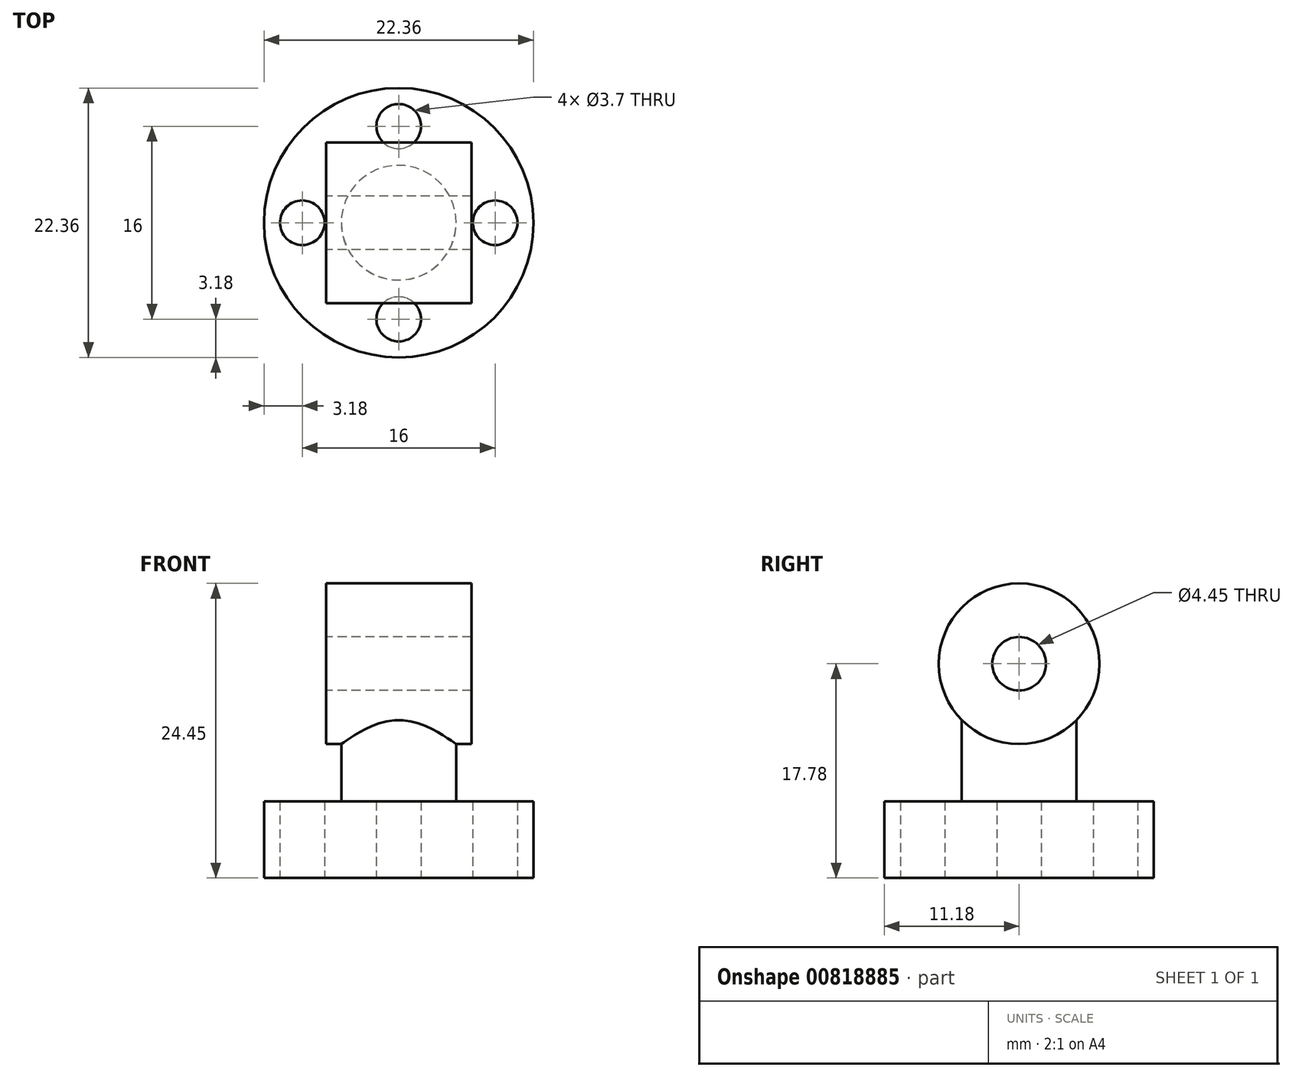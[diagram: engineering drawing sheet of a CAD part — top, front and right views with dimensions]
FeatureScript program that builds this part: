
annotation { "Feature Type Name" : "Feature", "Feature Type Description" : "" }
export const myFeature = defineFeature(function(context is Context, id is Id, definition is map)
    precondition{}
    {
        {
            var Q0;
            Q0=qCreatedBy(makeId("Top.planeOp"),FACE);
            var sketch = newSketch(context, id + "F0", { "sketchPlane" : qUnion([Q0])});
            skCircle(sketch, "E0", {"center": v(0, 0) * mm, "radius": 11.18 * mm});
            skLineSegment(sketch, "E1", {"start": v(0, 0) * mm, "end": v(0, 8) * mm});
            skCircle(sketch, "E2", {"center": v(0, 8) * mm, "radius": 1.85 * mm});
            skCircle(sketch, "E3.1.0", {"center": v(8, 0) * mm, "radius": 1.85 * mm});
            skCircle(sketch, "E3.2.0", {"center": v(0, -8) * mm, "radius": 1.85 * mm});
            skCircle(sketch, "E3.3.0", {"center": v(-8, 0) * mm, "radius": 1.85 * mm});
            skLineSegment(sketch, "E3.anchor1", {"start": v(0, 0) * mm, "end": v(0, 8) * mm, "construction": true});
            skLineSegment(sketch, "E3.anchor2", {"start": v(0, 0) * mm, "end": v(-8, 0) * mm, "construction": true});
            skSolve(sketch);
        }
        {
            var Q0;
            Q0=makeQuery(id+"F0.imprint","IMPRINT",FACE,{"disambiguationData":[TD([[makeQuery(id+"F0.imprint","IMPRINT",EDGE,{"derivedFrom":sQuery(id+"F0.wireOp",EDGE,"E0")}),1.0]])]});
            extrude(context, id + "F1", {"entities" : qUnion([Q0]), "depth" : 6.35 * mm, "offsetDistance" : 25.4 * mm});
        }
        {
            var Q0;
            Q0=makeQuery(id+"F1.opExtrude","CAP_FACE",FACE,{"disambiguationData":[OSD([sQuery(id+"F0.wireOp",EDGE,"E0"),sQuery(id+"F0.wireOp",EDGE,"E2"),sQuery(id+"F0.wireOp",EDGE,"E3.1.0"),sQuery(id+"F0.wireOp",EDGE,"E3.2.0"),sQuery(id+"F0.wireOp",EDGE,"E3.3.0")])],"isStart":false});
            var sketch = newSketch(context, id + "F2", { "sketchPlane" : qUnion([Q0])});
            skCircle(sketch, "E4", {"center": v(0, 0) * mm, "radius": 4.76 * mm});
            skSolve(sketch);
        }
        {
            var Q0;
            Q0=makeQuery(id+"F2.imprint","IMPRINT",FACE,{"disambiguationData":[TD([[makeQuery(id+"F2.imprint","IMPRINT",EDGE,{"derivedFrom":sQuery(id+"F2.wireOp",EDGE,"E4")}),1.0]])]});
            extrude(context, id + "F3", {"entities" : qUnion([Q0]), "operationType" : NewBodyOperationType.ADD, "depth" : 8.25 * mm, "offsetDistance" : 25.4 * mm});
        }
        {
            var Q0;
            Q0=qCreatedBy(makeId("Right.planeOp"),FACE);
            var sketch = newSketch(context, id + "F4", { "sketchPlane" : qUnion([Q0])});
            skLineSegment(sketch, "E5", {"start": v(0, 0) * mm, "end": v(0, 6.35) * mm});
            skLineSegment(sketch, "E6", {"start": v(0, 6.35) * mm, "end": v(0, 17.78) * mm});
            skCircle(sketch, "E7", {"center": v(0, 17.78) * mm, "radius": 6.67 * mm});
            skCircle(sketch, "E8", {"center": v(0, 17.78) * mm, "radius": 2.22 * mm});
            skSolve(sketch);
        }
        {
            var Q0;
            Q0=makeQuery(id+"F4.imprint","IMPRINT",FACE,{"disambiguationData":[TD([[makeQuery(id+"F4.imprint","IMPRINT",EDGE,{"derivedFrom":sQuery(id+"F4.wireOp",EDGE,"E7")}),1.0]])]});
            extrude(context, id + "F5", {"entities" : qUnion([Q0]), "operationType" : NewBodyOperationType.ADD, "endBound" : BoundingType.SYMMETRIC, "depth" : 12.06 * mm, "offsetDistance" : 25.4 * mm});
        }
    });
